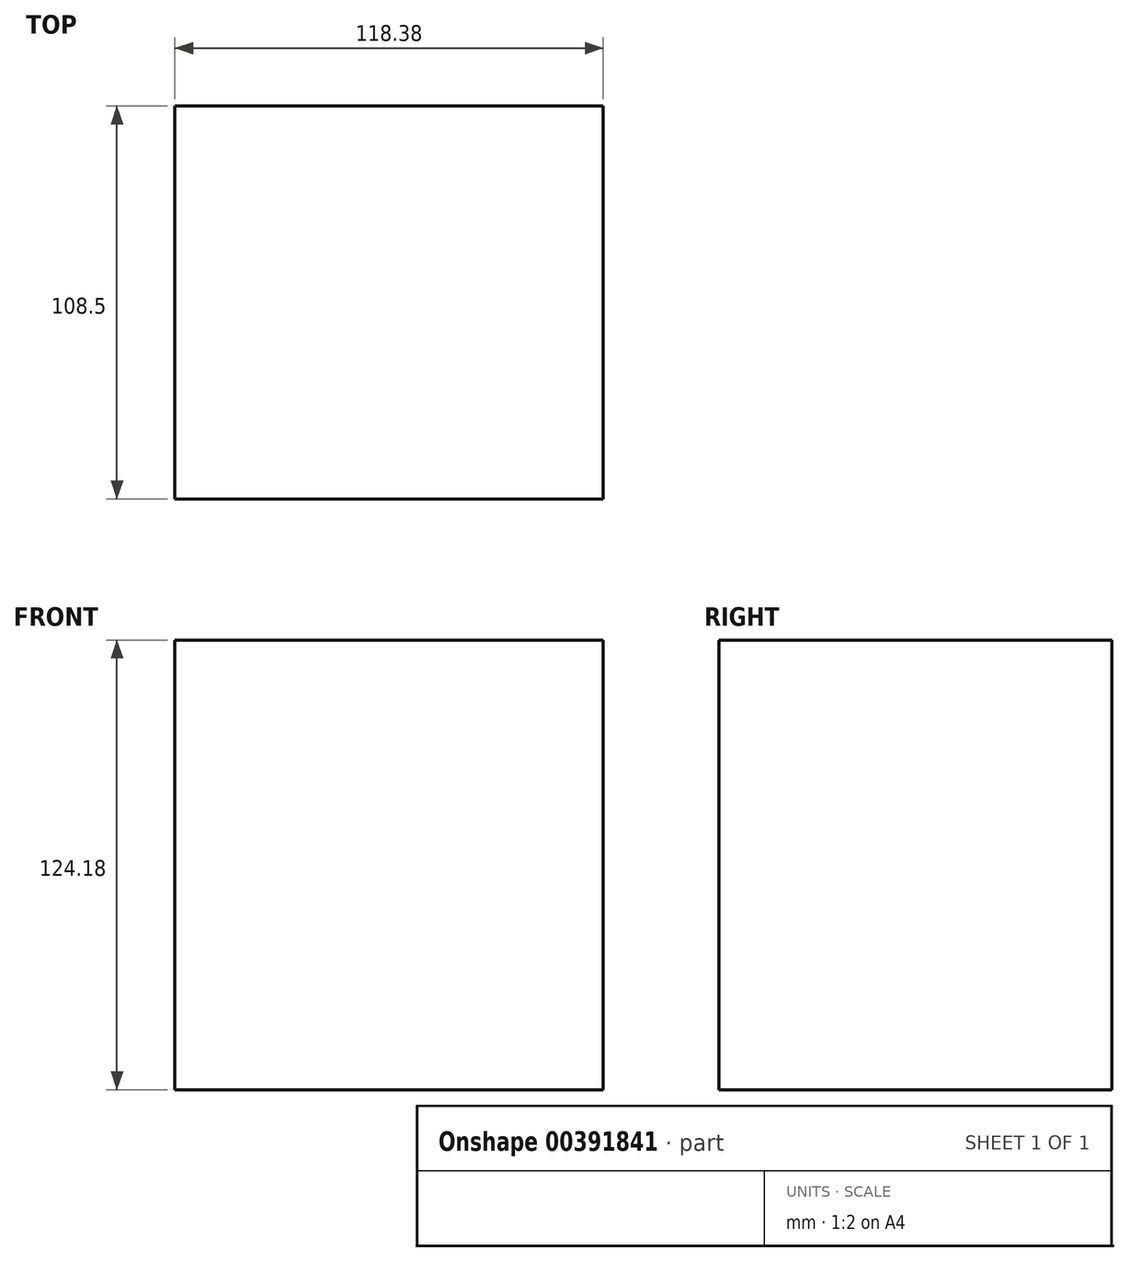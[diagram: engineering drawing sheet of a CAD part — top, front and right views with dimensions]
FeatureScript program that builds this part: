
annotation { "Feature Type Name" : "Feature", "Feature Type Description" : "" }
export const myFeature = defineFeature(function(context is Context, id is Id, definition is map)
    precondition{}
    {
        {
            var Q0;
            Q0=qCreatedBy(makeId("Top.planeOp"),FACE);
            var sketch = newSketch(context, id + "F0", { "sketchPlane" : qUnion([Q0])});
            skLineSegment(sketch, "E0.bottom", {"start": v(-42.07, -42.96) * mm, "end": v(76.31, -42.96) * mm});
            skLineSegment(sketch, "E0.top", {"start": v(-42.07, 65.54) * mm, "end": v(76.31, 65.54) * mm});
            skLineSegment(sketch, "E0.left", {"start": v(-42.07, -42.96) * mm, "end": v(-42.07, 65.54) * mm});
            skLineSegment(sketch, "E0.right", {"start": v(76.31, -42.96) * mm, "end": v(76.31, 65.54) * mm});
            skSolve(sketch);
        }
        {
            var Q0;
            Q0=makeQuery(id+"F0.imprint","IMPRINT",FACE,{"disambiguationData":[TD([[makeQuery(id+"F0.imprint","IMPRINT",EDGE,{"derivedFrom":sQuery(id+"F0.wireOp",EDGE,"E0.bottom")}),1.0]])]});
            extrude(context, id + "F1", {"entities" : qUnion([Q0]), "depth" : 124.18 * mm});
        }
    });
